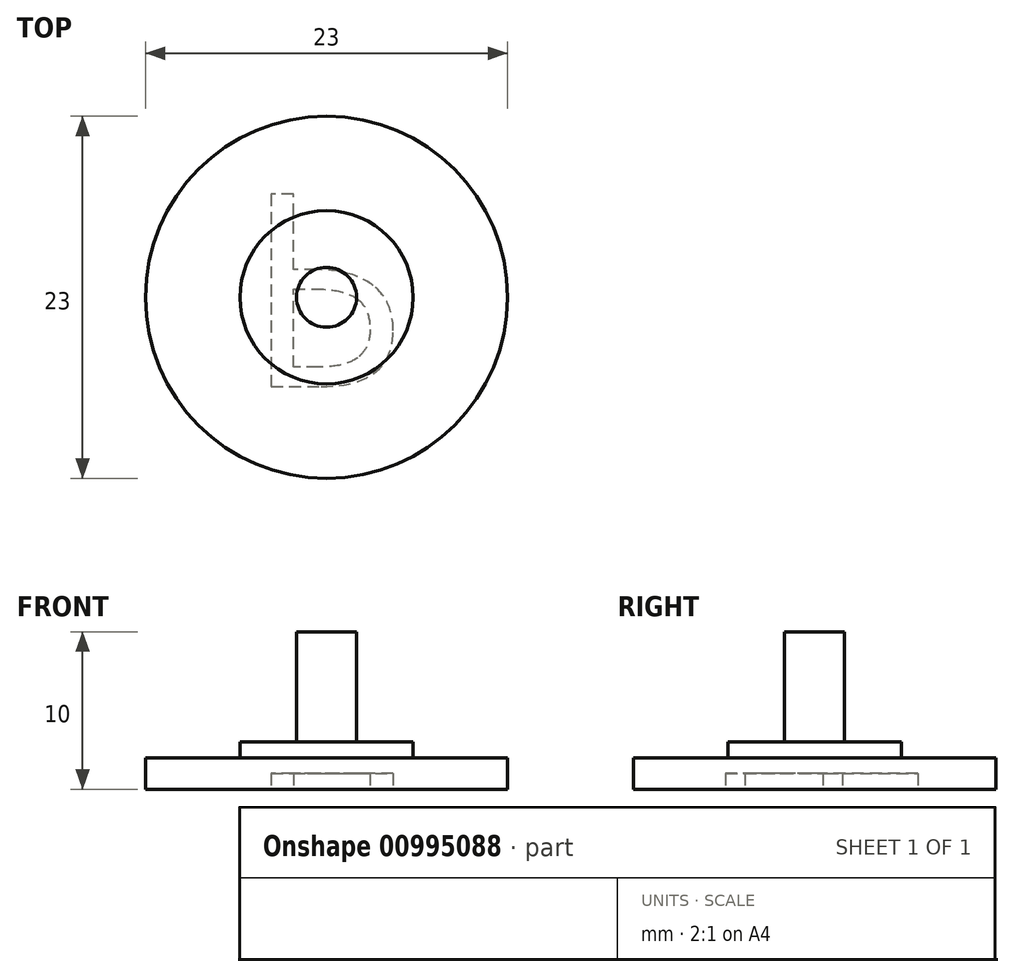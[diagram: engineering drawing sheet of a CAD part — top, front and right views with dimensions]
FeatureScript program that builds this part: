
annotation { "Feature Type Name" : "Feature", "Feature Type Description" : "" }
export const myFeature = defineFeature(function(context is Context, id is Id, definition is map)
    precondition{}
    {
        {
            var Q0;
            Q0=qCreatedBy(makeId("Top.planeOp"),FACE);
            var sketch = newSketch(context, id + "F0", { "sketchPlane" : qUnion([Q0])});
            skCircle(sketch, "E0", {"center": v(0, 0) * mm, "radius": 11.5 * mm});
            skSolve(sketch);
        }
        {
            var Q0;
            Q0 = qSketchRegion(id + "F0", true);
            extrude(context, id + "F1", {"entities" : qUnion([Q0]), "depth" : 2 * mm, "offsetDistance" : 25 * mm});
        }
        {
            var Q0;
            Q0=makeQuery(id+"F1.opExtrude","CAP_FACE",FACE,{"disambiguationData":[OSD([sQuery(id+"F0.wireOp",EDGE,"E0")])],"isStart":false});
            var sketch = newSketch(context, id + "F2", { "sketchPlane" : qUnion([Q0])});
            skCircle(sketch, "E1", {"center": v(0, 0) * mm, "radius": 5.5 * mm});
            skSolve(sketch);
        }
        {
            var Q0;
            Q0=makeQuery(id+"F2.imprint","IMPRINT",FACE,{"disambiguationData":[TD([[makeQuery(id+"F2.imprint","IMPRINT",EDGE,{"derivedFrom":sQuery(id+"F2.wireOp",EDGE,"E1")}),1.0]])]});
            extrude(context, id + "F3", {"entities" : qUnion([Q0]), "operationType" : NewBodyOperationType.ADD, "depth" : 1 * mm, "offsetDistance" : 25 * mm});
        }
        {
            var Q0;
            Q0=makeQuery(id+"F3.opExtrude","CAP_FACE",FACE,{"disambiguationData":[OSD([sQuery(id+"F2.wireOp",EDGE,"E1")])],"isStart":false});
            var sketch = newSketch(context, id + "F4", { "sketchPlane" : qUnion([Q0])});
            skCircle(sketch, "E2", {"center": v(0, 0) * mm, "radius": 1.9 * mm});
            skSolve(sketch);
        }
        {
            var Q0;
            Q0 = qSketchRegion(id + "F4", true);
            extrude(context, id + "F5", {"entities" : qUnion([Q0]), "operationType" : NewBodyOperationType.ADD, "depth" : 7 * mm, "offsetDistance" : 25 * mm});
        }
        {
            var Q0;
            Q0=makeQuery(id+"F1.opExtrude","CAP_FACE",FACE,{"disambiguationData":[OSD([sQuery(id+"F0.wireOp",EDGE,"E0")])],"isStart":true});
            var sketch = newSketch(context, id + "F6", { "sketchPlane" : qUnion([Q0])});
            skText(sketch, "E3", { "text": "P", "fontName": "OpenSans-Regular.ttf"});
            const initialGuessF6  = {"E3": [-0.0052, -0.00656, 1, 0, 0.01233]};
            skSetInitialGuess(sketch, initialGuessF6);
            skSolve(sketch);
        }
        {
            var Q0;
            Q0=makeQuery(id+"F6.imprint","IMPRINT",FACE,{"disambiguationData":[TD([[makeQuery(id+"F6.imprint","IMPRINT",EDGE,{"derivedFrom":sQuery(id+"F6.wireOp",EDGE,"E3.sketch_text.stroke-0")}),-1.0]])]});
            extrude(context, id + "F7", {"entities" : qUnion([Q0]), "operationType" : NewBodyOperationType.REMOVE, "oppositeDirection" : true, "depth" : 1 * mm, "offsetDistance" : 25 * mm});
        }
    });
